# Revit family: Shower_Outlet_Elbow-GROHE-Movario-28484_Series
name_source: partatom
category: Plumbing Fixtures
units: mm (PartAtom-declared; Revit-internal decimal feet)

## family parameters
Cut with Voids When Loaded = No
Host = Face
OmniClass Number = 23.45.05.14.17
OmniClass Title = Showers
Part Type = Normal
Room Calculation Point = No
Round Connector Dimension = Use Diameter
Shared = Yes

## types (2) — shared parameters
CW Connection = No
CWFU = 3
Default Elevation = 0"
Description = MOVARIO® WALL UNION WITH HAND SHOWER HOLDER
HW Connection = No
HWFU = 3
Height = 2 9/16"
Installation Type = Wall Mounted
Length = 3 11/16"
Manufacturer = Grohe
Price = Prices may vary. Please consult Manufacturer Representative for most up-to-date price list.
Product Documentation Link = https://americanstandard.box.com
Product Page URL = https://www.grohe.us
Revised Date = 04/26/2022
Tempered Connection Diameter = 1/2"
Tempered Connection Radius = 1/4"
Tempered Water Connection = Yes
URL = https://www.grohe.us
Vent Connection = No
WFU = 4
Warranty Documentation Link = https://cdn.cloud.grohe.com
Waste Connection = No
Width = 2 9/16"

## per-type parameters (varying)
| type | Assembly Code | Finish | Material |
| 28484EN0 | D2090800 | Metal-Grohe-EN0-Brushed Nickel | Metal-Grohe-EN0-Brushed Nickel |
| 28484000 | D2010710 | Metal-Grohe-000-Chrome | Metal-Grohe-000-Chrome |

note: column(s) folded — value = type name in every type: Model

## geometry (parser evidence)
native form markers: Sweep x3
no freeform markers — native parametric forms only
